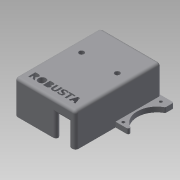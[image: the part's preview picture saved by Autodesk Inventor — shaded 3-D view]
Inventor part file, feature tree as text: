
AUTODESK INVENTOR PART (.ipt)
format: ipt  version: 2015 SP1 (Build 190203100, 203)  size: 1,432,576 bytes
history: native  units: mm
features: extrude x21, sketch x21, projected_geometry x16, fillet x9, reference x2, plane x1, mirror x1
ambient origin geometry x8: Origin, YZ Plane, XZ Plane, XY Plane, X Axis, Y Axis, Z Axis, Center Point
bodies: Solid1 (feature_tree)
feature tree (71):
  extrude  "Extrusion1"  Depth=60.0mm
  extrude  "Extrusion3"  Depth=20.0mm TaperAngle=0.0deg
  extrude  "Extrusion4"  Depth=3.5mm TaperAngle=0.0deg
  extrude  "Extrusion5"  Depth=3.5mm TaperAngle=0.0deg
  extrude  "Extrusion6"  Depth=6.0mm
  extrude  "Extrusion7"  Depth=2.0mm
  extrude  "Extrusion8"  Depth=2.0mm
  fillet  "Fillet1"  Radius=2.0mm
  extrude  "Extrusion9"  Depth=3.5mm TaperAngle=0.0deg
  extrude  "Extrusion10"  Depth=2.0mm TaperAngle=0.0deg
  fillet  "Fillet2"  Radius=3.5mm
  extrude  "Extrusion11"  Depth=3.5mm TaperAngle=0.0deg
  extrude  "Extrusion12"  Depth=3.5mm TaperAngle=0.0deg
  extrude  "Extrusion13"  Depth=1.25mm
  extrude  "Extrusion14"  Depth=16.0mm
  sketch  "Sketch19"  dims[d76=3.5mm d77=3.5mm]
  fillet  "Fillet3"  Radius=3.5mm
  extrude  "Extrusion16"  Depth=3.5mm
  extrude  "Extrusion17"  Depth=12.5mm
  extrude  "Extrusion18"  Depth=3.5mm TaperAngle=0.0deg
  extrude  "Extrusion19"  Depth=2.0mm TaperAngle=0.0deg
  fillet  "Fillet5"  Radius=2.0mm
  fillet  "Fillet6"  Radius=1.0mm
  fillet  "Fillet7"  Radius=2.0mm
  fillet  "Fillet8"  Radius=1.0mm
  fillet  "Fillet9"  Radius=1.0mm
  fillet  "Fillet10"  Radius=1.0mm
  plane  "Work Plane1"
  mirror  "Mirror1"
  extrude  "Extrusion20"  Depth=10.0mm TaperAngle=0.0deg
  extrude  "Extrusion21"  Depth=10.0mm TaperAngle=0.0deg
  extrude  "Extrusion22"  [1 undecoded]
  extrude  "Extrusion23"  [1 undecoded]
  sketch  "Sketch1"  dims[d0=42.5mm d1=60.0mm]
  sketch  "Sketch4"  dims[d2=3.5mm d3=0.0mm d11=20.0mm d12=0.0mm]
  sketch  "Sketch5"  dims[d13=3.5mm d14=0.0mm d15=3.5mm d16=0.0mm]
  sketch  "Sketch6"  dims[d17=3.5mm d18=0.0mm d19=3.5mm d20=0.0mm]
  sketch  "Sketch7"  dims[d21=6.0mm d22=6.0mm]
  reference  "Reference1"
  sketch  "Sketch8"  dims[d23=3.5mm d24=2.0mm]
  reference  "Reference2"
  sketch  "Sketch11"  dims[d25=2.0mm d26=2.0mm d27=2.0mm]
  projected_geometry  "Projected Loop1"
  projected_geometry  "Projected Loop2"
  projected_geometry  "Projected Loop3"
  sketch  "Sketch12"  dims[d28=3.5mm d29=3.5mm d30=0.0mm]
  sketch  "Sketch13"  dims[d31=2.0mm d32=3.5mm d33=0.0mm d34=3.5mm d35=0.0mm]
  projected_geometry  "Projected Loop4"
  projected_geometry  "Projected Loop5"
  projected_geometry  "Projected Loop6"
  projected_geometry  "Projected Loop7"
  projected_geometry  "Projected Loop8"
  sketch  "Sketch15"  dims[d36=3.0mm d51=3.5mm d52=0.0mm]
  sketch  "Sketch16"  dims[d53=3.5mm d54=0.0mm d55=3.5mm d56=0.0mm]
  sketch  "Sketch17"  dims[d57=3.5mm d58=0.0mm d70=1.25mm]
  sketch  "Sketch18"  dims[d71=11.75mm d72=16.0mm d73=3.5mm d74=0.0mm]
  sketch  "Sketch21"  dims[d78=25.0mm d79=12.5mm]
  projected_geometry  "Projected Loop10"
  sketch  "Sketch22"  dims[d80=20.0mm d81=3.5mm d82=0.0mm]
  projected_geometry  "Projected Loop11"
  sketch  "Sketch23"  dims[d92=3.5mm d93=0.0mm d94=3.5mm d95=0.0mm d96=2.0mm d97=1.0mm d98=2.0mm d99=1.0mm d100=1.0mm d101=1.0mm]
  projected_geometry  "Projected Loop12"
  sketch  "Sketch24"  dims[d102=56.25mm d103=10.0mm d104=0.0mm]
  sketch  "Sketch25"  dims[d105=10.0mm d106=0.0mm d107=10.0mm d108=0.0mm]
  sketch  "Sketch26"  dims[d109=2.0mm d110=0.0mm]
  projected_geometry  "Projected Loop13"
  projected_geometry  "Projected Loop14"
  projected_geometry  "Projected Loop15"
  projected_geometry  "Projected Loop16"
  projected_geometry  "Projected Loop17"
  sketch  "Sketch27"
note: 2 required parameter values undecoded (feature->parameter linkage not recoverable at this tier; creation-order binding heuristic only, values carry confidence <= 0.55)
